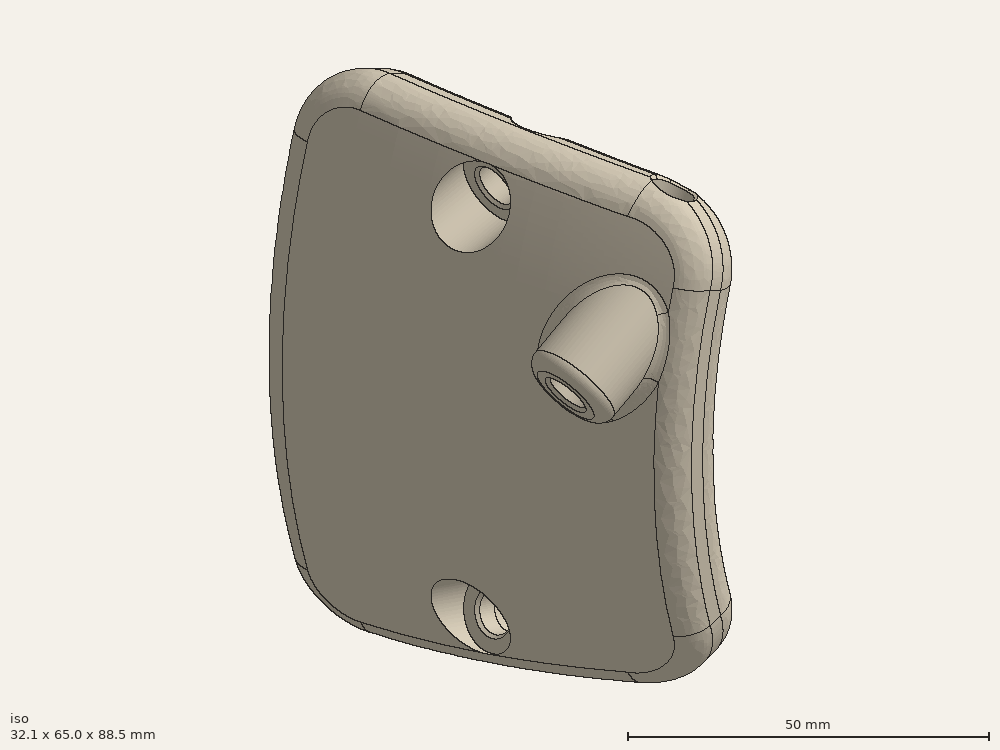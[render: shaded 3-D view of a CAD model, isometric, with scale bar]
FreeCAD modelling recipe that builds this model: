
FCSTD DOCUMENT  (FreeCAD 0.17R13541 (Git))
Label: left_patch_circular_seal
License: All rights reserved
LicenseURL: http://en.wikipedia.org/wiki/All_rights_reserved
objects: Sketcher::SketchObject×15, PartDesign::Plane×6, PartDesign::Fillet×6, PartDesign::Pocket×5, PartDesign::Line×2, PartDesign::Pad×2, PartDesign::SubtractiveLoft×2, PartDesign::Groove×2, PartDesign::Chamfer×2, PartDesign::Revolution×1, PartDesign::SubtractivePipe×1, PartDesign::Mirrored×1, PartDesign::Body×1
note: 59 computed .brp shape members not serialized (recipe doc carries the construction recipe); baked Part::Feature solids carry a one-line shape summary decoded from their .brp

FEATURE [Sketcher::SketchObject] Sketch
  MapMode = 5
  Support = -> [XY_Plane]
  sketch-geometry (14):
    g0: LineSegment StartX=-103 StartY=0 StartZ=0 EndX=-90 EndY=0 EndZ=0
    g1: LineSegment StartX=-121 StartY=65 StartZ=0 EndX=-108 EndY=65 EndZ=0
    g2: Circle [constr] CenterX=-121 CenterY=65 CenterZ=0 NormalX=0 NormalY=0 NormalZ=1 AngleXU=0 Radius=1
    g3: Circle [constr] CenterX=-119 CenterY=32.5 CenterZ=0 NormalX=0 NormalY=0 NormalZ=1 AngleXU=0 Radius=1
    g4: Circle [constr] CenterX=-103 CenterY=0 CenterZ=0 NormalX=0 NormalY=0 NormalZ=1 AngleXU=0 Radius=1
    g5: BSplineCurve PolesCount=3 KnotsCount=2 Degree=2 IsPeriodic=0
    g6: GeomPoint [constr] X=-121 Y=65 Z=0
    g7: GeomPoint [constr] X=-103 Y=0 Z=0
    g8: Circle [constr] CenterX=-108 CenterY=65 CenterZ=0 NormalX=0 NormalY=0 NormalZ=1 AngleXU=0 Radius=1
    g9: Circle [constr] CenterX=-105 CenterY=32.5 CenterZ=0 NormalX=0 NormalY=0 NormalZ=1 AngleXU=0 Radius=1
    g10: Circle [constr] CenterX=-90 CenterY=0 CenterZ=0 NormalX=0 NormalY=0 NormalZ=1 AngleXU=0 Radius=1
    g11: BSplineCurve PolesCount=3 KnotsCount=2 Degree=2 IsPeriodic=0
    g12: GeomPoint [constr] X=-108 Y=65 Z=0
    g13: GeomPoint [constr] X=-90 Y=0 Z=0
  constraints (32):
    c: Horizontal(g0)
    c: Horizontal(g1)
    c: Coincident(g2,g1)
    c: Radius(g2) = 1
    c: Equal(g2,g3)
    c: Equal(g2,g4)
    c: Coincident(g4,g0)
    c: InternalAlignment(g2,g5)
    c: InternalAlignment(g3,g5)
    c: InternalAlignment(g4,g5)
    c: InternalAlignment(g6,g5)
    c: InternalAlignment(g7,g5)
    c: Coincident(g8,g1)
    c: Radius(g8) = 1
    c: Equal(g8,g9)
    c: Equal(g8,g10)
    c: Coincident(g10,g0)
    c: InternalAlignment(g8,g11)
    c: InternalAlignment(g9,g11)
    c: InternalAlignment(g10,g11)
    c: InternalAlignment(g12,g11)
    c: InternalAlignment(g13,g11)
    c: DistanceX(g1,g1) = 13  'upper thickness'
    c: DistanceX(g0,g0) = 13  'lower thickness'
    c: DistanceY(g0,g1) = 65
    c: DistanceY(g0,g-1) = 0
    c: DistanceY(g0,g9) = 32.5
    c: DistanceY(g0,g3) = 32.5
    c: DistanceX(g0,g-1) = 90  'lower radius'
    c: DistanceX(g3,g9) = 14  'middle thickness'
    c: DistanceX(g9,g0) = 15  'middle radius difference'
    c: DistanceX(g1,g0) = 18  'upper radius difference'
FEATURE [PartDesign::Revolution] Revolution
  Angle = 45
  Axis = (0,1,0)
  Base = (0,0,0)
  Midplane = true
  Profile = -> Sketch
  ReferenceAxis = -> Sketch [V_Axis]
FEATURE [PartDesign::Line] DatumLine
  AttacherType = Attacher::AttachEngineLine
  AttachmentOffset = pos=(60,0,0) rot=(0,1,0;0.279253rad)
  MapMode = 29
  Placement = pos=(0,60,0) rot=(0.470251,0.624045,0.624045;2.26246rad)
  Support = -> [X_Axis]
FEATURE [PartDesign::Plane] DatumPlane001
  AttachmentOffset = pos=(0,0,-98) rot=(0,0,1;0rad)
  MapMode = 2
  Placement = pos=(-94.2036,32.9875,0) rot=(0.470251,0.624045,0.624045;2.26246rad)
  Support = -> [DatumLine]
FEATURE [Sketcher::SketchObject] Sketch017
  MapMode = 5
  Placement = pos=(-94.2036,32.9875,0) rot=(0.470251,0.624045,0.624045;2.26246rad)
  Support = -> [DatumPlane001]
  sketch-geometry (1):
    g0: Circle CenterX=0 CenterY=0 CenterZ=0 NormalX=0 NormalY=0 NormalZ=1 AngleXU=0 Radius=19
  constraints (2):
    c: Coincident(g0,g-1)
    c: Radius(g0) = 19
FEATURE [PartDesign::Pad] Pad001
  BaseFeature = -> Revolution
  Length = 20
  Length2 = 100
  Profile = -> Sketch017
  Type = 3
  UpToFace = -> Revolution [Face3]
FEATURE [Sketcher::SketchObject] Sketch018
  ExternalGeometry = -> [DatumLine]
  MapMode = 5
  Support = -> [XY_Plane]
  sketch-geometry (12):
    g0: LineSegment [constr] StartX=-100.16 StartY=31.2796 StartZ=0 EndX=-94.5921 EndY=11.8621 EndZ=0
    g1: LineSegment [constr] StartX=-94.5921 StartY=11.8621 StartZ=0 EndX=-95.7456 EndY=11.5313 EndZ=0
    g2: LineSegment [constr] StartX=-95.7456 StartY=11.5313 StartZ=0 EndX=-99.8802 EndY=25.9503 EndZ=0
    g3: LineSegment [constr] StartX=-99.8802 StartY=25.9503 StartZ=0 EndX=-100.841 EndY=25.6746 EndZ=0
    g4: LineSegment [constr] StartX=-100.841 StartY=25.6746 StartZ=0 EndX=-101.668 EndY=28.5584 EndZ=0
    g5: LineSegment [constr] StartX=-101.668 StartY=28.5584 StartZ=0 EndX=-91.8635 EndY=31.3699 EndZ=0
    g6: LineSegment [constr] StartX=-91.8635 StartY=31.3699 StartZ=0 EndX=-86.902 EndY=14.0672 EndZ=0
    g7: LineSegment [constr] StartX=-86.902 StartY=14.0672 StartZ=0 EndX=-94.5921 EndY=11.8621 EndZ=0
    g8: LineSegment StartX=-96.2866 StartY=17.0458 StartZ=0 EndX=-81.8677 EndY=21.1804 EndZ=0
    g9: LineSegment StartX=-81.8677 StartY=21.1804 StartZ=0 EndX=-80.076 EndY=14.9322 EndZ=0
    g10: LineSegment StartX=-80.076 StartY=14.9322 StartZ=0 EndX=-94.495 EndY=10.7976 EndZ=0
    g11: ArcOfCircle CenterX=-95.3908 CenterY=13.9217 CenterZ=0 NormalX=0 NormalY=0 NormalZ=1 AngleXU=0 Radius=3.25 StartAngle=1.85005 EndAngle=4.99164
  constraints (35):
    c: PointOnObject(g0,g-3)
    c: Perpendicular(g-3,g0)
    c: Distance(g0) = 20.2
    c: Coincident(g0,g1)
    c: Coincident(g1,g2)
    c: Coincident(g2,g3)
    c: Coincident(g3,g4)
    c: Coincident(g4,g5)
    c: Coincident(g5,g6)
    c: Coincident(g6,g7)
    c: Coincident(g7,g1)
    c: Perpendicular(g0,g1)
    c: Perpendicular(g0,g3)
    c: Perpendicular(g0,g5)
    c: Perpendicular(g0,g7)
    c: Parallel(g6,g0)
    c: Parallel(g2,g0)
    c: Parallel(g4,g0)
    c: Distance(g1) = 1.2
    c: Distance(g2) = 15
    c: Distance(g3) = 1
    c: DistanceX(g0) = -100.16
    c: Distance(g6) = 18
    c: Distance(g7) = 8
    c: Coincident(g8,g9)
    c: Coincident(g9,g10)
    c: Tangent(g11,g8) = 1.5708
    c: Tangent(g11,g10) = 1.5708
    c: Parallel(g-3,g8)
    c: Parallel(g-3,g10)
    c: Perpendicular(g-3,g9)
    c: Distance(g9) = 6.5
    c: Distance(g11,g2) = 1
    c: Distance(g11,g-3) = 18
    c: Distance(g10) = 15
FEATURE [PartDesign::SubtractivePipe] SubtractivePipe
  AuxilleryCurvelinear = true
  AuxillerySpineTangent = false
  BaseFeature = -> Pad001
  Binormal = (0,0,0)
  Mode = 0
  Profile = -> Sketch018
  Refine = true
  Spine = -> Pad001 [Edge13,Edge14]
  SpineTangent = false
  Transformation = 0
  Transition = 0
FEATURE [Sketcher::SketchObject] Sketch019
  MapMode = 5
  Placement = pos=(-94.2036,32.9875,0) rot=(0.470251,0.624045,0.624045;2.26246rad)
  Support = -> [DatumPlane001]
  sketch-geometry (1):
    g0: Circle CenterX=0 CenterY=0 CenterZ=0 NormalX=0 NormalY=0 NormalZ=1 AngleXU=0 Radius=16
  constraints (2):
    c: Coincident(g0,g-1)
    c: Radius(g0) = 16
FEATURE [PartDesign::Plane] DatumPlane002
  AttachmentOffset = pos=(0,0,-18) rot=(0,0,1;0rad)
  MapMode = 4
  Placement = pos=(4.96147,42.6973,0) rot=(-0.515639,-0.684276,-0.515639;1.9414rad)
  Support = -> [DatumLine]
FEATURE [Sketcher::SketchObject] Sketch027
  MapMode = 5
  Placement = pos=(4.96147,42.6973,0) rot=(-0.515639,-0.684276,-0.515639;1.9414rad)
  Support = -> [DatumPlane002]
  sketch-geometry (1):
    g0: Circle CenterX=0 CenterY=-113.122 CenterZ=0 NormalX=0 NormalY=0 NormalZ=1 AngleXU=0 Radius=1.5
  constraints (2):
    c: PointOnObject(g0,g-2)
    c: Radius(g0) = 1.5
FEATURE [PartDesign::Plane] DatumPlane003
  AttachmentOffset = pos=(0,0,0) rot=(0,1,0;0.05236rad)
  MapMode = 5
  Placement = pos=(0,0,0) rot=(0,1,0;0.05236rad)
  Support = -> [XY_Plane]
FEATURE [PartDesign::Plane] DatumPlane004
  AttachmentOffset = pos=(0,0,123) rot=(0,-1,0;0.785398rad)
  MapMode = 5
  Placement = pos=(0,0,123) rot=(0,-1,0;0.785398rad)
  Support = -> [XY_Plane]
FEATURE [PartDesign::Line] DatumLine001
  AttacherType = Attacher::AttachEngineLine
  AttachmentOffset = pos=(5,0,-21) rot=(1,0,0;1.5708rad)
  MapMode = 16
  Placement = pos=(5.78838,39.8135,5) rot=(0.137845,-0.980815,0.137845;1.59017rad)
  Support = -> [DatumLine]
FEATURE [PartDesign::Fillet] Fillet019
  Base = -> SubtractivePipe [Edge7,Edge6,Edge10,Edge9]
  BaseFeature = -> SubtractivePipe
  Radius = 12
FEATURE [PartDesign::Pocket] Pocket007
  BaseFeature = -> Fillet019
  Length = 30
  Length2 = 100
  Midplane = true
  Profile = -> Sketch019
  Refine = true
  Type = 0
FEATURE [Sketcher::SketchObject] Sketch020
  ExternalGeometry = -> [Pocket007]
  MapMode = 5
  Placement = pos=(-92.725,-26.5885,0) rot=(0.470251,0.624045,0.624045;2.26246rad)
  Support = -> [Pocket007]
  sketch-geometry (2):
    g0: Circle CenterX=57.6757 CenterY=0 CenterZ=0 NormalX=0 NormalY=0 NormalZ=1 AngleXU=0 Radius=16
    g1: Circle CenterX=57.6757 CenterY=0 CenterZ=0 NormalX=0 NormalY=0 NormalZ=1 AngleXU=0 Radius=18
  constraints (4):
    c: Coincident(g0,g-3)
    c: Coincident(g1,g0)
    c: Radius(g0) = 16
    c: Radius(g1) = 18
FEATURE [PartDesign::Pocket] Pocket008
  BaseFeature = -> Pocket007
  Length = 2
  Length2 = 2
  Profile = -> Sketch020
  Refine = true
  Type = 4
FEATURE [PartDesign::Fillet] Fillet  label="Vorderkannte innen"
  Base = -> Pocket008 [Edge12,Edge11]
  BaseFeature = -> Pocket008
  Radius = 5
FEATURE [PartDesign::Fillet] Fillet015  label="Vorderkante aussen"
  Base = -> Fillet [Edge13]
  BaseFeature = -> Fillet
  Radius = 5
FEATURE [Sketcher::SketchObject] Sketch025
  MapMode = 5
  Placement = pos=(0,0,0) rot=(0,1,0;0.392699rad)
  Support = -> [Fillet015]
  sketch-geometry (1):
    g0: Circle CenterX=-100.7 CenterY=10 CenterZ=0 NormalX=0 NormalY=0 NormalZ=1 AngleXU=0 Radius=3.1
  constraints (3):
    c: Radius(g0) = 3.1
    c: DistanceY(g-1,g0) = 10
    c: DistanceX(g0,g-1) = 100.7
FEATURE [PartDesign::Pocket] Pocket012
  BaseFeature = -> Fillet015
  Length = 6
  Length2 = 100
  Profile = -> Sketch025
  Type = 0
FEATURE [PartDesign::Pocket] Pocket013
  BaseFeature = -> Pocket012
  Length = 3
  Length2 = 0.5
  Profile = -> Sketch027
  Type = 4
FEATURE [PartDesign::Plane] DatumPlane
  AttachmentOffset = pos=(0,0,-95) rot=(0,1,0;0.523599rad)
  MapMode = 5
  Placement = pos=(-54.5,0,-90.47) rot=(0,1,0;1.0472rad)
  Support = -> [Pocket013]
FEATURE [Sketcher::SketchObject] Sketch028
  MapMode = 5
  Placement = pos=(-54.5,0,-90.47) rot=(0,1,0;1.0472rad)
  Support = -> [DatumPlane]
  sketch-geometry (1):
    g0: Circle CenterX=-120 CenterY=10 CenterZ=0 NormalX=0 NormalY=0 NormalZ=1 AngleXU=0 Radius=7
  constraints (3):
    c: Radius(g0) = 7
    c: DistanceY(g-1,g0) = 10
    c: DistanceX(g0,g-1) = 120
FEATURE [PartDesign::Pad] Pad
  BaseFeature = -> Pocket013
  Length = 30
  Length2 = 100
  Profile = -> Sketch028
  Type = 2
FEATURE [PartDesign::Plane] DatumPlane005
  AttachmentOffset = pos=(0,0,-32.5) rot=(0,0,1;0rad)
  MapMode = 5
  Placement = pos=(0,32.5,3e-12) rot=(1,0,0;1.5708rad)
  Support = -> [XZ_Plane]
FEATURE [Sketcher::SketchObject] Sketch036
  MapMode = 5
  Placement = pos=(0,32.5,3e-12) rot=(1,0,0;1.5708rad)
  Support = -> [DatumPlane005]
  sketch-geometry (8):
    g0: LineSegment StartX=-118.637 StartY=30.6472 StartZ=0 EndX=-80 EndY=41 EndZ=0
    g1: LineSegment StartX=-80 StartY=41 StartZ=0 EndX=-81.4882 EndY=46.5541 EndZ=0
    g2: LineSegment StartX=-81.4882 StartY=46.5541 StartZ=0 EndX=-103.705 EndY=40.6012 EndZ=0
    g3: LineSegment StartX=-103.705 StartY=40.6012 StartZ=0 EndX=-103.032 EndY=38.0898 EndZ=0
    g4: LineSegment StartX=-103.032 StartY=38.0898 StartZ=0 EndX=-106.895 EndY=37.0546 EndZ=0
    g5: LineSegment StartX=-106.895 StartY=37.0546 StartZ=0 EndX=-107.568 EndY=39.566 EndZ=0
    g6: LineSegment StartX=-107.568 StartY=39.566 StartZ=0 EndX=-120.125 EndY=36.2013 EndZ=0
    g7: LineSegment StartX=-120.125 StartY=36.2013 StartZ=0 EndX=-118.637 EndY=30.6472 EndZ=0
  constraints (24):
    c: Coincident(g0,g1)
    c: Coincident(g1,g2)
    c: Parallel(g2,g0)
    c: Perpendicular(g0,g1)
    c: Coincident(g2,g3)
    c: Coincident(g3,g4)
    c: Coincident(g4,g5)
    c: Parallel(g5,g1)
    c: Parallel(g4,g0)
    c: Parallel(g1,g3)
    c: Coincident(g5,g6)
    c: Coincident(g6,g7)
    c: Coincident(g7,g0)
    c: Parallel(g7,g1)
    c: Parallel(g6,g0)
    c: Angle(g-1,g0) = 0.261799
    c: Distance(g4) = 4
    c: Distance(g3,g0) = 3.15
    c: Distance(g7) = 5.75
    c: Distance(g6) = 13
    c: Distance(g0) = 40
    c: Distance(g1) = 5.75
    c: DistanceX(g0) = -80
    c: DistanceY(g0) = 41
FEATURE [Sketcher::SketchObject] Sketch037
  ExternalGeometry = -> [Pad]
  MapMode = 5
  Placement = pos=(-80.0497,0,-46.2167) rot=(-0.654654,0.654654,0.377964;3.86433rad)
  Support = -> [Pad]
  sketch-geometry (1):
    g0: Circle CenterX=-10 CenterY=68.9007 CenterZ=0 NormalX=0 NormalY=0 NormalZ=1 AngleXU=0 Radius=3.1
  constraints (2):
    c: Coincident(g0,g-3)
    c: Radius(g0) = 3.1
FEATURE [PartDesign::Pocket] Pocket
  BaseFeature = -> Pad
  Length = 6
  Length2 = 100
  Profile = -> Sketch037
  Refine = true
  Type = 0
FEATURE [Sketcher::SketchObject] Sketch038
  ExternalGeometry = -> [Pocket]
  MapMode = 5
  Placement = pos=(-2.2961,0,-5.54328) rot=(0,1,0;0.392699rad)
  Support = -> [Pocket]
  sketch-geometry (1):
    g0: Circle CenterX=-100.7 CenterY=10 CenterZ=0 NormalX=0 NormalY=0 NormalZ=1 AngleXU=0 Radius=1.5
  constraints (2):
    c: Coincident(g0,g-3)
    c: Radius(g0) = 1.5
FEATURE [Sketcher::SketchObject] Sketch039
  ExternalGeometry = -> [Pocket]
  MapMode = 5
  Placement = pos=(-74.8535,0,-43.2167) rot=(0.654654,-0.654654,-0.377964;2.41886rad)
  Support = -> [Pocket]
  sketch-geometry (1):
    g0: Circle CenterX=-10 CenterY=68.9007 CenterZ=0 NormalX=0 NormalY=0 NormalZ=1 AngleXU=0 Radius=1.5
  constraints (2):
    c: Coincident(g0,g-3)
    c: Radius(g0) = 1.5
FEATURE [PartDesign::SubtractiveLoft] SubtractiveLoft
  BaseFeature = -> Pocket
  Closed = false
  Profile = -> Sketch038
  Refine = true
  Ruled = true
  Sections = -> [Sketch039]
FEATURE [Sketcher::SketchObject] Sketch033
  MapMode = 5
  Placement = pos=(-10.1092,35.2549,0) rot=(-0.09889,0.703641,0.703641;3.33873rad)
  Support = -> [SubtractiveLoft]
  sketch-geometry (1):
    g0: Circle CenterX=96.5841 CenterY=0 CenterZ=0 NormalX=0 NormalY=0 NormalZ=1 AngleXU=0 Radius=1.5
  constraints (1):
    c: Radius(g0) = 1.5
FEATURE [PartDesign::Groove] Groove
  Angle = 90
  Axis = (-0.961262,-0.275637,0)
  Base = (5.78838,39.8135,5)
  BaseFeature = -> SubtractiveLoft
  Profile = -> Sketch033
  ReferenceAxis = -> DatumLine001
FEATURE [Sketcher::SketchObject] Sketch034
  ExternalGeometry = -> [Groove]
  MapMode = 5
  Placement = pos=(-2.2961,0,-5.54328) rot=(0,1,0;0.392699rad)
  Support = -> [Groove]
  sketch-geometry (1):
    g0: Circle CenterX=-100.7 CenterY=10 CenterZ=0 NormalX=0 NormalY=0 NormalZ=1 AngleXU=0 Radius=1.51
  constraints (2):
    c: Coincident(g0,g-3)
    c: Radius(g0) = 1.51
FEATURE [Sketcher::SketchObject] Sketch035
  ExternalGeometry = -> [Groove]
  MapMode = 5
  Placement = pos=(-1e-12,0,5) rot=(1,0,0;3.14159rad)
  Support = -> [Groove]
  sketch-geometry (1):
    g0: Circle CenterX=-101.574 CenterY=-3.82646 CenterZ=0 NormalX=0 NormalY=0 NormalZ=1 AngleXU=0 Radius=1.5
  constraints (1):
    c: Radius(g0) = 1.5
FEATURE [PartDesign::SubtractiveLoft] SubtractiveLoft001
  BaseFeature = -> Groove
  Closed = false
  Profile = -> Sketch035
  Refine = true
  Ruled = true
  Sections = -> [Sketch034]
FEATURE [PartDesign::Chamfer] Chamfer
  Base = -> SubtractiveLoft001 [Edge55,Edge78]
  BaseFeature = -> SubtractiveLoft001
  Size = 0.5
FEATURE [PartDesign::Fillet] Fillet017
  Base = -> Chamfer [Edge90]
  BaseFeature = -> Chamfer
  Radius = 2
FEATURE [PartDesign::Fillet] Fillet018
  Base = -> Fillet017 [Edge4]
  BaseFeature = -> Fillet017
  Radius = 2
FEATURE [PartDesign::Groove] Groove001
  Angle = 360
  Axis = (0.965926,0,0.258819)
  Base = (-118.637,32.5,30.6472)
  BaseFeature = -> Fillet018
  Profile = -> Sketch036
  ReferenceAxis = -> Sketch036 [Edge1]
  Refine = true
  Reversed = true
FEATURE [PartDesign::Mirrored] Mirrored
  BaseFeature = -> Groove001
  MirrorPlane = -> XY_Plane
  Originals = -> [Groove001]
  Refine = true
FEATURE [PartDesign::Chamfer] Chamfer001
  Base = -> Mirrored [Face43,Face50]
  BaseFeature = -> Mirrored
  Size = 0.5
FEATURE [PartDesign::Fillet] Fillet020
  Base = -> Chamfer001 [Edge108,Edge129]
  BaseFeature = -> Chamfer001
  Radius = 0.3
FEATURE [PartDesign::Body] Body
  Group = -> [Sketch,Revolution,DatumLine,DatumPlane001,Sketch017,Pad001,Sketch018,SubtractivePipe,Sketch019,Fillet019,Pocket007,Sketch020,Pocket008,Fillet,Fillet015,DatumPlane,Sketch025,Pocket012,DatumPlane002,Sketch027,Pocket013,Sketch028,Pad,Sketch037,Pocket,Sketch038,Sketch039,DatumPlane003,DatumPlane004,Sketch033,DatumLine001,SubtractiveLoft,Groove,Sketch034,Sketch035,SubtractiveLoft001,Chamfer,Fillet017,+7 more]
  Origin = -> Origin
  Tip = -> Fillet020
